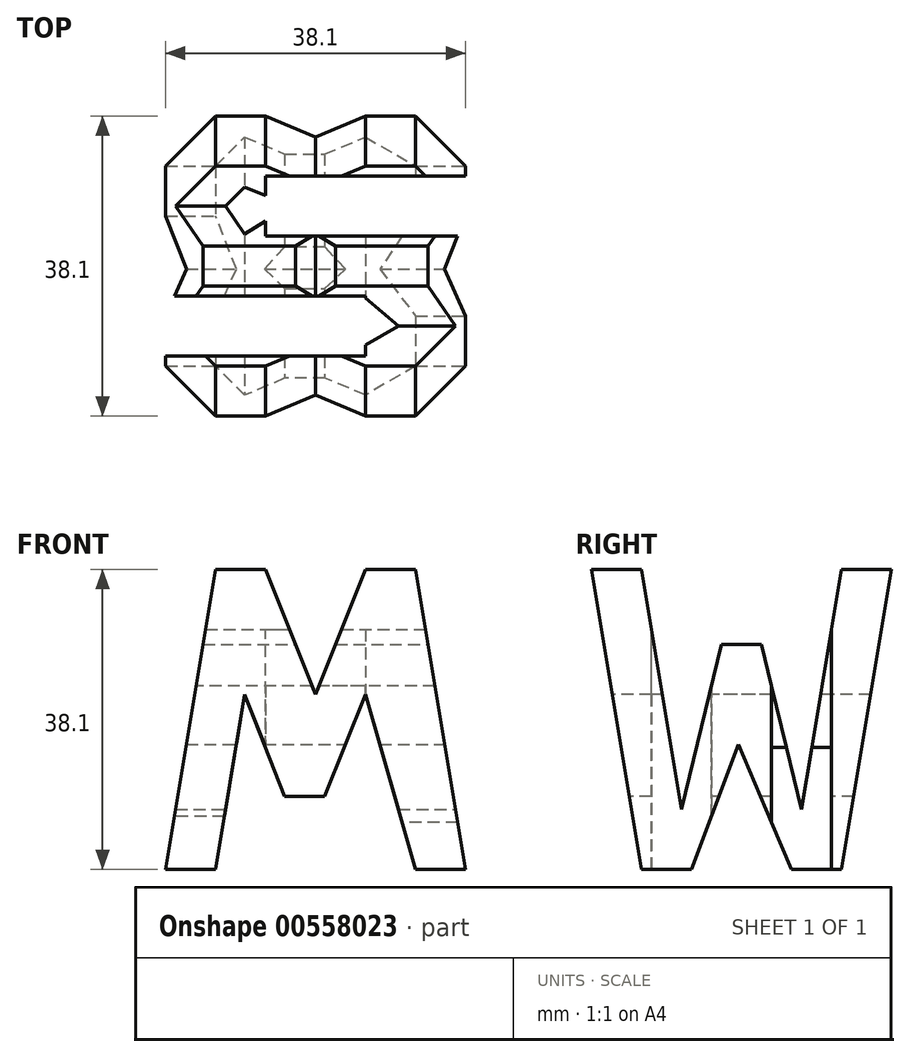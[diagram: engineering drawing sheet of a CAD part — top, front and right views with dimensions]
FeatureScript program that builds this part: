
annotation { "Feature Type Name" : "Feature", "Feature Type Description" : "" }
export const myFeature = defineFeature(function(context is Context, id is Id, definition is map)
    precondition{}
    {
        {
            var Q0;
            Q0=qCreatedBy(makeId("Front.planeOp"),FACE);
            var sketch = newSketch(context, id + "F0", { "sketchPlane" : qUnion([Q0])});
            skLineSegment(sketch, "E0", {"start": v(0, 0) * mm, "end": v(0, 38.1) * mm});
            skLineSegment(sketch, "E1", {"start": v(0, 38.1) * mm, "end": v(38.1, 38.1) * mm});
            skLineSegment(sketch, "E2", {"start": v(38.1, 38.1) * mm, "end": v(38.1, 0) * mm});
            skLineSegment(sketch, "E3", {"start": v(38.1, 0) * mm, "end": v(0, 0) * mm});
            skSolve(sketch);
        }
        {
            var Q0;
            Q0 = qSketchRegion(id + "F0", true);
            extrude(context, id + "F1", {"entities" : qUnion([Q0]), "depth" : 38.1 * mm, "offsetDistance" : 25.4 * mm});
        }
        {
            var Q0;
            Q0=qCreatedBy(makeId("Front.planeOp"),FACE);
            cPlane(context, id + "F2", {"entities" : qUnion([Q0]), "cplaneType" : CPlaneType.OFFSET, "offset" : 38.1 * mm, "width" : 152.4 * mm, "height" : 152.4 * mm});
        }
        {
            var Q0;
            Q0=qCreatedBy(makeId("Right.planeOp"),FACE);
            cPlane(context, id + "F3", {"entities" : qUnion([Q0]), "cplaneType" : CPlaneType.OFFSET, "offset" : 38.1 * mm, "width" : 152.4 * mm, "height" : 152.4 * mm});
        }
        {
            var Q0;
            Q0=qCreatedBy(makeId("Top.planeOp"),FACE);
            cPlane(context, id + "F4", {"entities" : qUnion([Q0]), "cplaneType" : CPlaneType.OFFSET, "offset" : 38.1 * mm, "width" : 152.4 * mm, "height" : 152.4 * mm});
        }
        {
            var Q0;
            Q0=qCreatedBy(id+"F3.planeOp",FACE);
            var sketch = newSketch(context, id + "F5", { "sketchPlane" : qUnion([Q0])});
            skLineSegment(sketch, "E4", {"start": v(0, 0) * mm, "end": v(0, 38.1) * mm});
            skLineSegment(sketch, "E5", {"start": v(0, 38.1) * mm, "end": v(-38.1, 38.1) * mm});
            skLineSegment(sketch, "E6", {"start": v(-38.1, 38.1) * mm, "end": v(-38.1, 0) * mm});
            skLineSegment(sketch, "E7", {"start": v(-38.1, 0) * mm, "end": v(0, 0) * mm});
            skLineSegment(sketch, "E8", {"start": v(-38.1, 38.1) * mm, "end": v(-31.75, 0) * mm});
            skLineSegment(sketch, "E9", {"start": v(-25.4, 0) * mm, "end": v(-19.43, 15.88) * mm});
            skLineSegment(sketch, "E10", {"start": v(-19.43, 15.88) * mm, "end": v(-12.7, 0) * mm});
            skLineSegment(sketch, "E11", {"start": v(-6.35, 0) * mm, "end": v(0, 38.1) * mm});
            skLineSegment(sketch, "E12", {"start": v(-31.75, 38.1) * mm, "end": v(-26.67, 7.62) * mm});
            skLineSegment(sketch, "E13", {"start": v(-26.67, 7.62) * mm, "end": v(-21.59, 28.58) * mm});
            skLineSegment(sketch, "E14", {"start": v(-21.59, 28.58) * mm, "end": v(-16.5, 28.58) * mm});
            skLineSegment(sketch, "E15", {"start": v(-16.5, 28.58) * mm, "end": v(-11.43, 7.62) * mm});
            skLineSegment(sketch, "E16", {"start": v(-11.43, 7.62) * mm, "end": v(-6.35, 38.1) * mm});
            skSolve(sketch);
        }
        {
            var Q0;
            {var subQ0=sQuery(id+"F5.wireOp",EDGE,"E12");Q0=makeQuery(id+"F5.imprint","IMPRINT",FACE,{"disambiguationData":[TD([[makeQuery(id+"F5.imprint","IMPRINT",EDGE,{"derivedFrom":subQ0}),1.0]])]});}
            var Q1;
            {var subQ0=sQuery(id+"F5.wireOp",EDGE,"E6");Q1=makeQuery(id+"F5.imprint","IMPRINT",FACE,{"disambiguationData":[TD([[makeQuery(id+"F5.imprint","IMPRINT",EDGE,{"derivedFrom":subQ0}),1.0]])]});}
            var Q2;
            {var subQ0=sQuery(id+"F5.wireOp",EDGE,"E9");Q2=makeQuery(id+"F5.imprint","IMPRINT",FACE,{"disambiguationData":[TD([[makeQuery(id+"F5.imprint","IMPRINT",EDGE,{"derivedFrom":subQ0}),-1.0]])]});}
            var Q3;
            {var subQ0=sQuery(id+"F5.wireOp",EDGE,"E4");Q3=makeQuery(id+"F5.imprint","IMPRINT",FACE,{"disambiguationData":[TD([[makeQuery(id+"F5.imprint","IMPRINT",EDGE,{"derivedFrom":subQ0}),1.0]])]});}
            extrude(context, id + "F6", {"entities" : qUnion([Q0, Q1, Q2, Q3]), "operationType" : NewBodyOperationType.REMOVE, "oppositeDirection" : true, "depth" : 38.1 * mm, "offsetDistance" : 25.4 * mm});
        }
        {
            var Q0;
            Q0=qCreatedBy(id+"F2.planeOp",FACE);
            var sketch = newSketch(context, id + "F7", { "sketchPlane" : qUnion([Q0])});
            skLineSegment(sketch, "E17", {"start": v(0, 0) * mm, "end": v(0, 38.1) * mm});
            skLineSegment(sketch, "E18", {"start": v(0, 38.1) * mm, "end": v(38.1, 38.1) * mm});
            skLineSegment(sketch, "E19", {"start": v(38.1, 38.1) * mm, "end": v(38.1, 0) * mm});
            skLineSegment(sketch, "E20", {"start": v(38.1, 0) * mm, "end": v(0, 0) * mm});
            skLineSegment(sketch, "E21", {"start": v(0, 0) * mm, "end": v(6.35, 38.1) * mm});
            skLineSegment(sketch, "E22", {"start": v(12.7, 38.1) * mm, "end": v(19.05, 22.23) * mm});
            skLineSegment(sketch, "E23", {"start": v(19.05, 22.23) * mm, "end": v(25.4, 38.1) * mm});
            skLineSegment(sketch, "E24", {"start": v(31.75, 38.1) * mm, "end": v(38.1, 0) * mm});
            skLineSegment(sketch, "E25", {"start": v(31.75, 0) * mm, "end": v(25.4, 22.23) * mm});
            skLineSegment(sketch, "E26", {"start": v(25.4, 22.23) * mm, "end": v(20.21, 9.26) * mm});
            skLineSegment(sketch, "E27", {"start": v(20.21, 9.26) * mm, "end": v(15.13, 9.26) * mm});
            skLineSegment(sketch, "E28", {"start": v(15.13, 9.26) * mm, "end": v(10.05, 22.23) * mm});
            skLineSegment(sketch, "E29", {"start": v(10.05, 22.23) * mm, "end": v(6.35, 0) * mm});
            skSolve(sketch);
        }
        {
            var Q0;
            {var subQ0=sQuery(id+"F7.wireOp",EDGE,"E25");Q0=makeQuery(id+"F7.imprint","IMPRINT",FACE,{"disambiguationData":[TD([[makeQuery(id+"F7.imprint","IMPRINT",EDGE,{"derivedFrom":subQ0}),1.0]])]});}
            var Q1;
            {var subQ0=sQuery(id+"F7.wireOp",EDGE,"E17");Q1=makeQuery(id+"F7.imprint","IMPRINT",FACE,{"disambiguationData":[TD([[makeQuery(id+"F7.imprint","IMPRINT",EDGE,{"derivedFrom":subQ0}),-1.0]])]});}
            var Q2;
            {var subQ0=sQuery(id+"F7.wireOp",EDGE,"E22");Q2=makeQuery(id+"F7.imprint","IMPRINT",FACE,{"disambiguationData":[TD([[makeQuery(id+"F7.imprint","IMPRINT",EDGE,{"derivedFrom":subQ0}),1.0]])]});}
            var Q3;
            {var subQ0=sQuery(id+"F7.wireOp",EDGE,"E19");Q3=makeQuery(id+"F7.imprint","IMPRINT",FACE,{"disambiguationData":[TD([[makeQuery(id+"F7.imprint","IMPRINT",EDGE,{"derivedFrom":subQ0}),-1.0]])]});}
            extrude(context, id + "F8", {"entities" : qUnion([Q0, Q1, Q2, Q3]), "operationType" : NewBodyOperationType.REMOVE, "oppositeDirection" : true, "depth" : 38.1 * mm, "offsetDistance" : 25.4 * mm});
        }
        {
            var Q0;
            Q0=qCreatedBy(id+"F4.planeOp",FACE);
            var sketch = newSketch(context, id + "F9", { "sketchPlane" : qUnion([Q0])});
            skLineSegment(sketch, "E30", {"start": v(0, 0) * mm, "end": v(0, -38.1) * mm});
            skLineSegment(sketch, "E31", {"start": v(0, -38.1) * mm, "end": v(38.1, -38.1) * mm});
            skLineSegment(sketch, "E32", {"start": v(38.1, -38.1) * mm, "end": v(38.1, 0) * mm});
            skLineSegment(sketch, "E33", {"start": v(38.1, 0) * mm, "end": v(0, 0) * mm});
            skLineSegment(sketch, "E34", {"start": v(38.1, -7.62) * mm, "end": v(12.7, -7.62) * mm});
            skLineSegment(sketch, "E35", {"start": v(12.7, -7.62) * mm, "end": v(12.7, -15.24) * mm});
            skLineSegment(sketch, "E36", {"start": v(12.7, -15.24) * mm, "end": v(38.1, -15.24) * mm});
            skLineSegment(sketch, "E37", {"start": v(0, -22.86) * mm, "end": v(25.4, -22.86) * mm});
            skPoint(sketch, "E37.endSnap0", {"position": v(0, -22.86) * mm});
            skLineSegment(sketch, "E38", {"start": v(25.4, -22.86) * mm, "end": v(25.4, -30.48) * mm});
            skLineSegment(sketch, "E39", {"start": v(25.4, -30.48) * mm, "end": v(0, -30.48) * mm});
            skSolve(sketch);
        }
        {
            var Q0;
            {var subQ0=sQuery(id+"F9.wireOp",EDGE,"E34");Q0=makeQuery(id+"F9.imprint","IMPRINT",FACE,{"disambiguationData":[TD([[makeQuery(id+"F9.imprint","IMPRINT",EDGE,{"derivedFrom":subQ0}),1.0]])]});}
            var Q1;
            {var subQ0=sQuery(id+"F9.wireOp",EDGE,"E37");Q1=makeQuery(id+"F9.imprint","IMPRINT",FACE,{"disambiguationData":[TD([[makeQuery(id+"F9.imprint","IMPRINT",EDGE,{"derivedFrom":subQ0}),-1.0]])]});}
            extrude(context, id + "F10", {"entities" : qUnion([Q0, Q1]), "operationType" : NewBodyOperationType.REMOVE, "oppositeDirection" : true, "depth" : 38.1 * mm, "offsetDistance" : 25.4 * mm});
        }
    });
